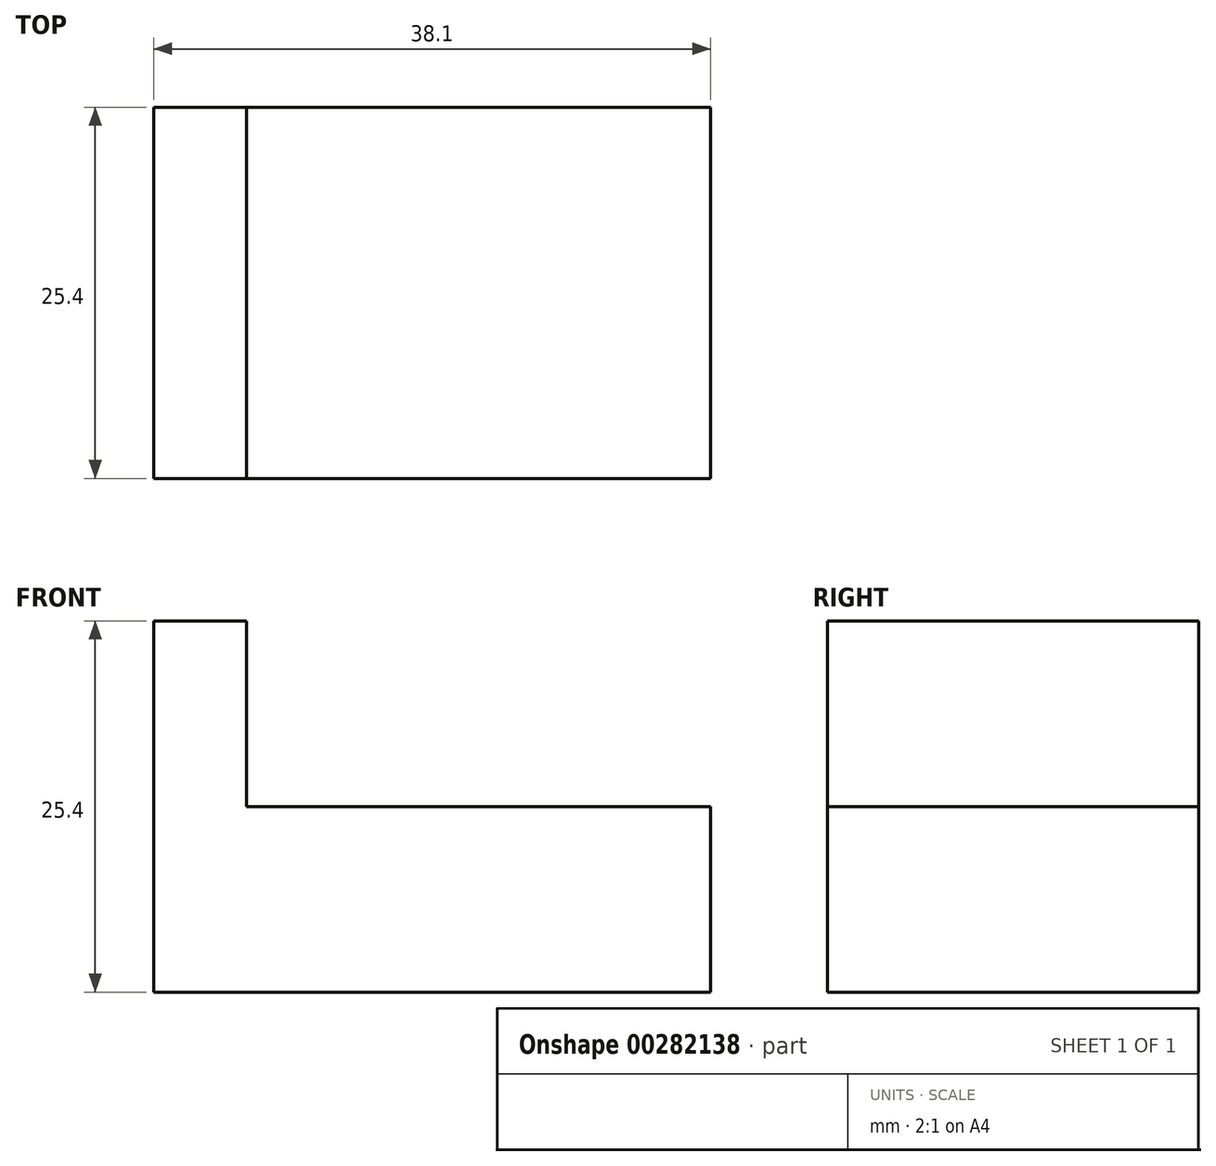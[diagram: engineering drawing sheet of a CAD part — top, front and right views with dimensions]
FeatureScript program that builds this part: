
annotation { "Feature Type Name" : "Feature", "Feature Type Description" : "" }
export const myFeature = defineFeature(function(context is Context, id is Id, definition is map)
    precondition{}
    {
        {
            var Q0;
            Q0=qCreatedBy(makeId("Front.planeOp"),FACE);
            var sketch = newSketch(context, id + "F0", { "sketchPlane" : qUnion([Q0])});
            skLineSegment(sketch, "E0.bottom", {"start": v(-19.05, 0) * mm, "end": v(19.05, 0) * mm});
            skLineSegment(sketch, "E0.top", {"start": v(-19.05, -12.7) * mm, "end": v(19.05, -12.7) * mm});
            skLineSegment(sketch, "E0.left", {"start": v(-19.05, 0) * mm, "end": v(-19.05, -12.7) * mm});
            skLineSegment(sketch, "E0.right", {"start": v(19.05, 0) * mm, "end": v(19.05, -12.7) * mm});
            skLineSegment(sketch, "E1.bottom", {"start": v(-19.05, 12.7) * mm, "end": v(-12.7, 12.7) * mm});
            skLineSegment(sketch, "E1.top", {"start": v(-19.05, 0) * mm, "end": v(-12.7, 0) * mm});
            skLineSegment(sketch, "E1.left", {"start": v(-19.05, 12.7) * mm, "end": v(-19.05, 0) * mm});
            skLineSegment(sketch, "E1.right", {"start": v(-12.7, 12.7) * mm, "end": v(-12.7, 0) * mm});
            skSolve(sketch);
        }
        {
            var Q0;
            Q0=makeQuery(id+"F0.imprint","IMPRINT",FACE,{"disambiguationData":[TD([[makeQuery(id+"F0.imprint","IMPRINT",EDGE,{"derivedFrom":sQuery(id+"F0.wireOp",EDGE,"E0.bottom")}),-1.0]])]});
            var Q1;
            Q1=sQuery(id+"F0.wireOp",EDGE,"E0.top");
            var Q2;
            Q2=sQuery(id+"F0.wireOp",EDGE,"E0.left");
            var Q3;
            Q3=sQuery(id+"F0.wireOp",EDGE,"E0.right");
            var Q4;
            Q4=sQuery(id+"F0.wireOp",EDGE,"E0.bottom");
            extrude(context, id + "F1", {"entities" : qUnion([Q0]), "surfaceEntities" : qUnion([Q1, Q2, Q3, Q4]), "depth" : 25.4 * mm});
        }
        {
            var Q0;
            Q0=makeQuery(id+"F0.imprint","IMPRINT",FACE,{"disambiguationData":[TD([[makeQuery(id+"F0.imprint","IMPRINT",EDGE,{"derivedFrom":sQuery(id+"F0.wireOp",EDGE,"E0.bottom")}),-1.0]])]});
            var Q1;
            Q1=makeQuery(id+"F0.imprint","IMPRINT",FACE,{"disambiguationData":[TD([[makeQuery(id+"F0.imprint","IMPRINT",EDGE,{"derivedFrom":sQuery(id+"F0.wireOp",EDGE,"E1.bottom")}),-1.0]])]});
            extrude(context, id + "F2", {"entities" : qUnion([Q0, Q1]), "operationType" : NewBodyOperationType.ADD, "depth" : 25.4 * mm});
        }
    });
